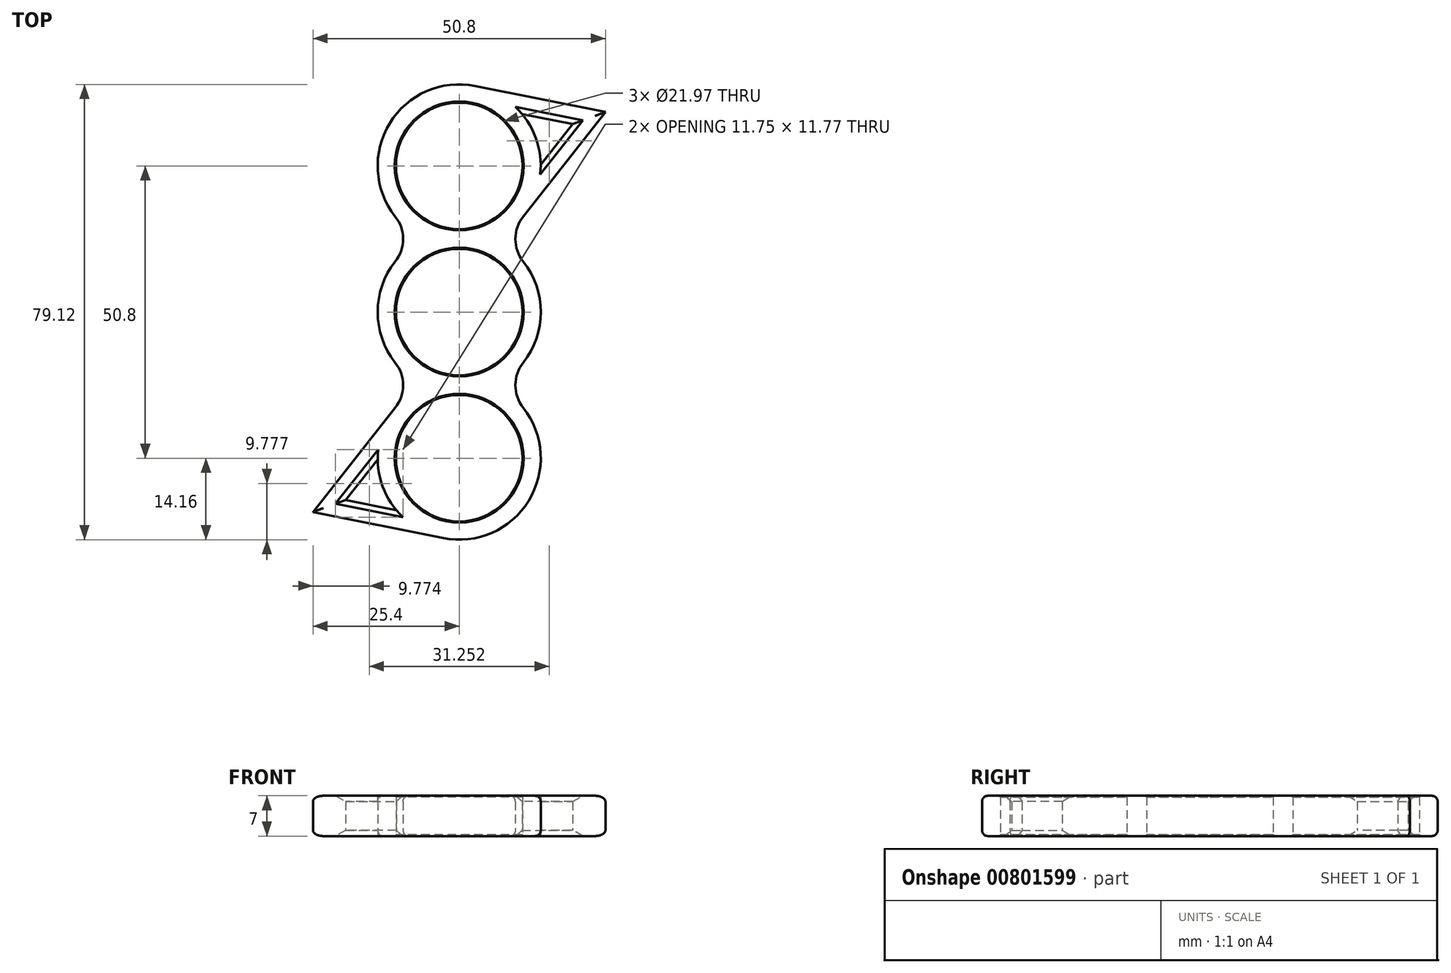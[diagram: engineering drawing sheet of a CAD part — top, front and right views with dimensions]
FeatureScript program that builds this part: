
annotation { "Feature Type Name" : "Feature", "Feature Type Description" : "" }
export const myFeature = defineFeature(function(context is Context, id is Id, definition is map)
    precondition{}
    {
        {
            var Q0;
            Q0=qCreatedBy(makeId("Top.planeOp"),FACE);
            var sketch = newSketch(context, id + "F0", { "sketchPlane" : qUnion([Q0])});
            skCircle(sketch, "E0", {"center": v(0, 0) * mm, "radius": 10.99 * mm});
            skCircle(sketch, "E1", {"center": v(0, 25.4) * mm, "radius": 10.99 * mm});
            skCircle(sketch, "E2", {"center": v(0, -25.4) * mm, "radius": 10.99 * mm});
            skLineSegment(sketch, "E3", {"start": v(0, 25.4) * mm, "end": v(0, -25.4) * mm, "construction": true});
            skLineSegment(sketch, "E4.bottom", {"start": v(-25.4, 57.15) * mm, "end": v(25.4, 57.15) * mm, "construction": true});
            skLineSegment(sketch, "E4.top", {"start": v(-25.4, -57.15) * mm, "end": v(25.4, -57.15) * mm, "construction": true});
            skLineSegment(sketch, "E4.left", {"start": v(-25.4, 57.15) * mm, "end": v(-25.4, -57.15) * mm, "construction": true});
            skLineSegment(sketch, "E4.right", {"start": v(25.4, 57.15) * mm, "end": v(25.4, -57.15) * mm, "construction": true});
            skPoint(sketch, "E5", {"position": v(0, 57.15) * mm});
            skPoint(sketch, "E6", {"position": v(-25.4, 0) * mm});
            skArc(sketch, "E7.0", {"start": v(-11.12, 8.77) * mm, "mid": v(-14.16, 0) * mm, "end": v(-11.12, -8.77) * mm});
            skArc(sketch, "E8.0", {"start": v(2.79, 39.28) * mm, "mid": v(-12.07, 32.8) * mm, "end": v(-11.12, 16.63) * mm});
            skArc(sketch, "E9.0", {"start": v(-2.79, -39.28) * mm, "mid": v(12.07, -32.8) * mm, "end": v(11.12, -16.63) * mm});
            skArc(sketch, "E10.trimOffspring", {"start": v(11.12, -8.77) * mm, "mid": v(14.16, 0) * mm, "end": v(11.12, 8.77) * mm});
            skPoint(sketch, "E11.visualSharp", {"position": v(-6.26, 12.7) * mm});
            skArc(sketch, "E11.filletArc", {"start": v(-11.12, 8.77) * mm, "mid": v(-9.76, 12.7) * mm, "end": v(-11.12, 16.63) * mm});
            skPoint(sketch, "E12.visualSharp", {"position": v(6.26, 12.7) * mm});
            skArc(sketch, "E12.filletArc", {"start": v(11.12, 16.63) * mm, "mid": v(9.76, 12.7) * mm, "end": v(11.12, 8.77) * mm});
            skPoint(sketch, "E13.visualSharp", {"position": v(-6.26, -12.7) * mm});
            skArc(sketch, "E13.filletArc", {"start": v(-11.12, -16.63) * mm, "mid": v(-9.76, -12.7) * mm, "end": v(-11.12, -8.77) * mm});
            skPoint(sketch, "E14.visualSharp", {"position": v(6.26, -12.7) * mm});
            skArc(sketch, "E14.filletArc", {"start": v(11.12, -8.77) * mm, "mid": v(9.76, -12.7) * mm, "end": v(11.12, -16.63) * mm});
            skLineSegment(sketch, "E15", {"start": v(2.79, 39.28) * mm, "end": v(25.4, 34.74) * mm});
            skLineSegment(sketch, "E16", {"start": v(25.4, 34.74) * mm, "end": v(11.12, 16.63) * mm});
            skLineSegment(sketch, "E17", {"start": v(-11.12, -16.63) * mm, "end": v(-25.4, -34.74) * mm});
            skLineSegment(sketch, "E18", {"start": v(-25.4, -34.74) * mm, "end": v(-2.79, -39.28) * mm});
            skArc(sketch, "E19", {"start": v(14.16, 25.61) * mm, "mid": v(13.3, 30.29) * mm, "end": v(10.92, 34.41) * mm});
            skLineSegment(sketch, "E20", {"start": v(10.92, 34.41) * mm, "end": v(19.7, 32.65) * mm});
            skLineSegment(sketch, "E21", {"start": v(19.7, 32.65) * mm, "end": v(14.16, 25.61) * mm});
            skArc(sketch, "E22", {"start": v(-14.16, -25.61) * mm, "mid": v(-13.3, -30.29) * mm, "end": v(-10.92, -34.41) * mm});
            skLineSegment(sketch, "E23", {"start": v(-14.16, -25.61) * mm, "end": v(-19.7, -32.65) * mm});
            skLineSegment(sketch, "E24", {"start": v(-19.7, -32.65) * mm, "end": v(-10.92, -34.41) * mm});
            skSolve(sketch);
        }
        {
            var Q0;
            Q0 = qSketchRegion(id + "F0", true);
            extrude(context, id + "F1", {"entities" : qUnion([Q0]), "depth" : 7 * mm, "offsetDistance" : 25.4 * mm});
        }
        {
            var Q0;
            Q0=makeQuery(id+"F1.opExtrude","CAP_EDGE",EDGE,{"disambiguationData":[OSD([sQuery(id+"F0.wireOp",EDGE,"E1")])],"isStart":false});
            var Q1;
            Q1=makeQuery(id+"F1.opExtrude","CAP_EDGE",EDGE,{"disambiguationData":[OSD([sQuery(id+"F0.wireOp",EDGE,"E0")])],"isStart":false});
            var Q2;
            Q2=makeQuery(id+"F1.opExtrude","CAP_EDGE",EDGE,{"disambiguationData":[OSD([sQuery(id+"F0.wireOp",EDGE,"E2")])],"isStart":false});
            var Q3;
            Q3=makeQuery(id+"F1.opExtrude","CAP_EDGE",EDGE,{"disambiguationData":[OSD([sQuery(id+"F0.wireOp",EDGE,"E1")])],"isStart":true});
            var Q4;
            Q4=makeQuery(id+"F1.opExtrude","CAP_EDGE",EDGE,{"disambiguationData":[OSD([sQuery(id+"F0.wireOp",EDGE,"E0")])],"isStart":true});
            var Q5;
            Q5=makeQuery(id+"F1.opExtrude","CAP_EDGE",EDGE,{"disambiguationData":[OSD([sQuery(id+"F0.wireOp",EDGE,"E2")])],"isStart":true});
            chamfer(context, id + "F2", {"entities" : qUnion([Q0, Q1, Q2, Q3, Q4, Q5]), "width" : .2 * mm, "tangentPropagation" : true});
        }
        {
            var Q0;
            Q0=makeQuery(id+"F1.opExtrude","CAP_EDGE",EDGE,{"disambiguationData":[OSD([sQuery(id+"F0.wireOp",EDGE,"E20")])],"isStart":false});
            var Q1;
            Q1=makeQuery(id+"F1.opExtrude","CAP_EDGE",EDGE,{"disambiguationData":[OSD([sQuery(id+"F0.wireOp",EDGE,"E21")])],"isStart":false});
            var Q2;
            Q2=makeQuery(id+"F1.opExtrude","CAP_EDGE",EDGE,{"disambiguationData":[OSD([sQuery(id+"F0.wireOp",EDGE,"E20")])],"isStart":true});
            var Q3;
            Q3=makeQuery(id+"F1.opExtrude","CAP_EDGE",EDGE,{"disambiguationData":[OSD([sQuery(id+"F0.wireOp",EDGE,"E21")])],"isStart":true});
            var Q4;
            Q4=makeQuery(id+"F1.opExtrude","CAP_EDGE",EDGE,{"disambiguationData":[OSD([sQuery(id+"F0.wireOp",EDGE,"E23")])],"isStart":false});
            var Q5;
            Q5=makeQuery(id+"F1.opExtrude","CAP_EDGE",EDGE,{"disambiguationData":[OSD([sQuery(id+"F0.wireOp",EDGE,"E24")])],"isStart":false});
            var Q6;
            Q6=makeQuery(id+"F1.opExtrude","CAP_EDGE",EDGE,{"disambiguationData":[OSD([sQuery(id+"F0.wireOp",EDGE,"E23")])],"isStart":true});
            var Q7;
            Q7=makeQuery(id+"F1.opExtrude","CAP_EDGE",EDGE,{"disambiguationData":[OSD([sQuery(id+"F0.wireOp",EDGE,"E24")])],"isStart":true});
            chamfer(context, id + "F3", {"entities" : qUnion([Q0, Q1, Q2, Q3, Q4, Q5, Q6, Q7]), "width" : 1 * mm, "tangentPropagation" : true});
        }
        {
            var Q0;
            Q0=makeQuery(id+"F1.opExtrude","CAP_EDGE",EDGE,{"disambiguationData":[OSD([sQuery(id+"F0.wireOp",EDGE,"E7.0")])],"isStart":true});
            var Q1;
            Q1=makeQuery(id+"F1.opExtrude","CAP_EDGE",EDGE,{"disambiguationData":[OSD([sQuery(id+"F0.wireOp",EDGE,"E9.0")])],"isStart":true});
            var Q2;
            Q2=makeQuery(id+"F1.opExtrude","CAP_EDGE",EDGE,{"disambiguationData":[OSD([sQuery(id+"F0.wireOp",EDGE,"E8.0")])],"isStart":false});
            var Q3;
            Q3=makeQuery(id+"F1.opExtrude","CAP_EDGE",EDGE,{"disambiguationData":[OSD([sQuery(id+"F0.wireOp",EDGE,"E16")])],"isStart":false});
            fillet(context, id + "F4", {"entities" : qUnion([Q0, Q1, Q2, Q3]), "radius" : 1 * mm, "tangentPropagation" : true, "allowEdgeOverflow" : false});
        }
    });
